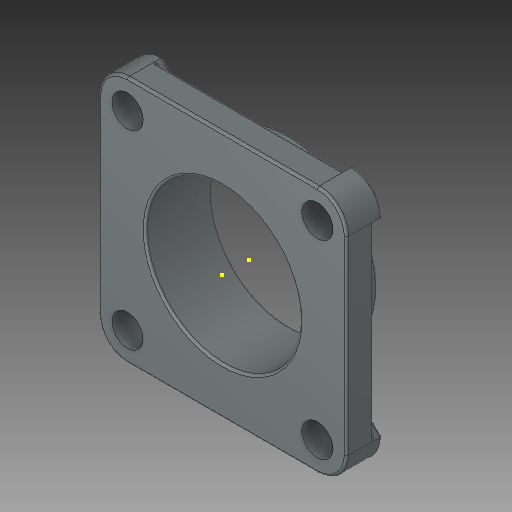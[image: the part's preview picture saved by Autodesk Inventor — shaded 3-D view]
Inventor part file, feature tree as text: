
AUTODESK INVENTOR PART (.ipt)
format: ipt  version: 2019 (Build 230136000, 136)  size: 448,512 bytes
history: native  units: in
note: dims shown in document units (in); Inventor stores cm internally (conversion verified against a paired STEP export)
features: sketch x10, other x3
ambient origin geometry x8: Origin, YZ Plane, XZ Plane, XY Plane, X Axis, Y Axis, Z Axis, Center Point
bodies: Solid1 (feature_tree)
feature tree (13):
  other  "project flange bearing part1.ipt"
  other  "Solid1::project flange bearing part1.ipt"
  other  "TaggingFeature1"
  sketch  "Sketch1"  dims[d0=0.3937in]
  sketch  "Sketch2"
  sketch  "Sketch3"
  sketch  "Sketch4"
  sketch  "Sketch5"
  sketch  "Sketch6"
  sketch  "Sketch7"
  sketch  "Sketch8"
  sketch  "Sketch9"
  sketch  "Sketch10"
